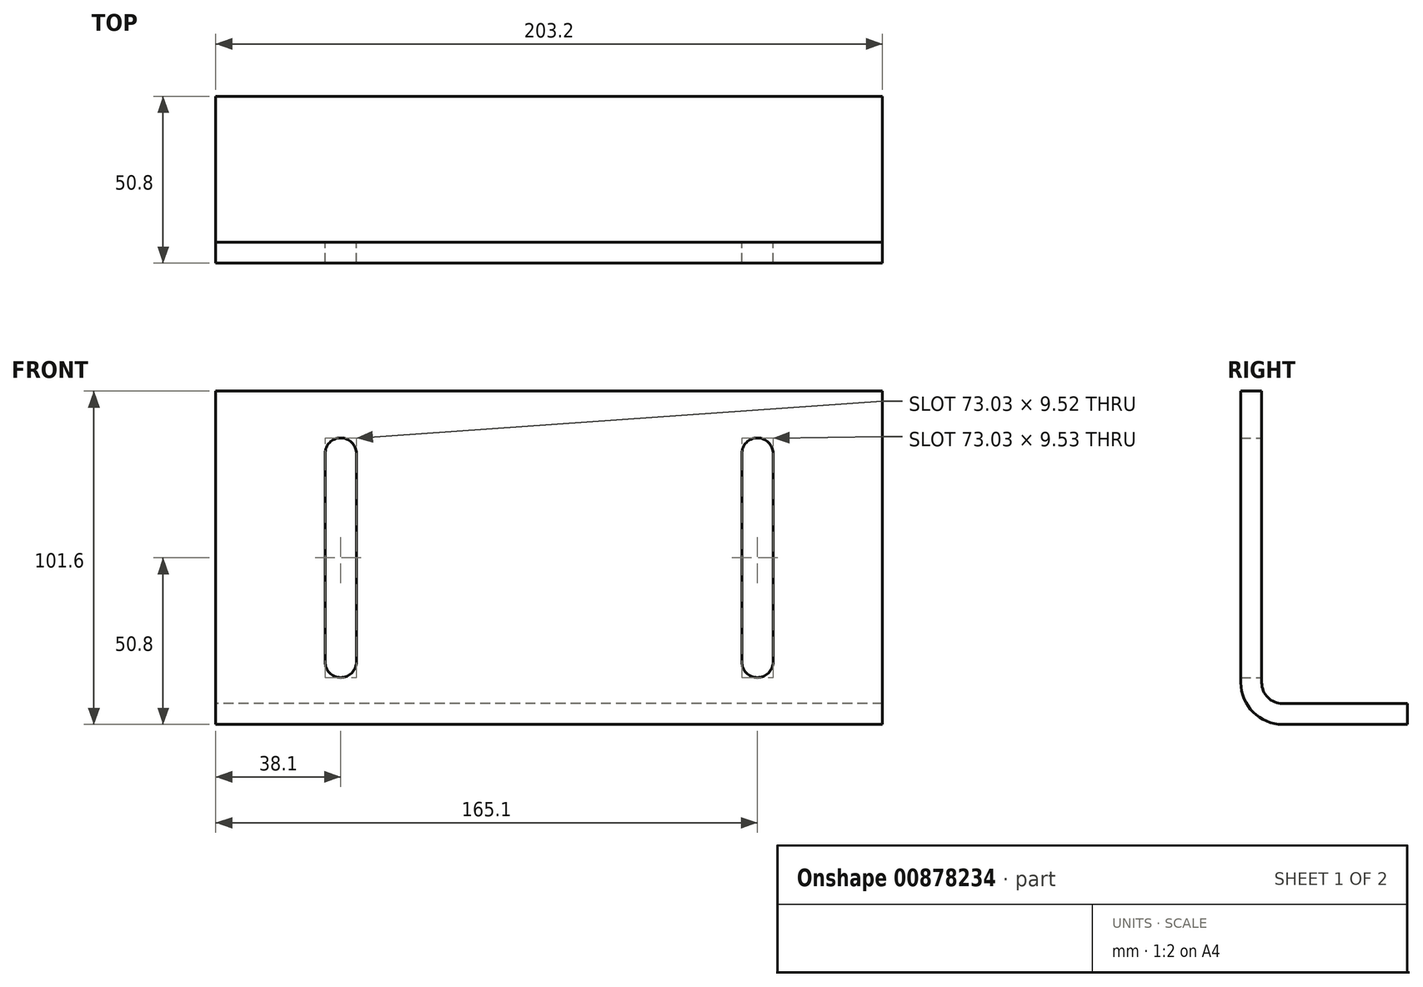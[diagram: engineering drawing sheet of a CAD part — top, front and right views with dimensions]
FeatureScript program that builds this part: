
annotation { "Feature Type Name" : "Feature", "Feature Type Description" : "" }
export const myFeature = defineFeature(function(context is Context, id is Id, definition is map)
    precondition{}
    {
        {
            var Q0;
            Q0=qCreatedBy(makeId("Right.planeOp"),FACE);
            var sketch = newSketch(context, id + "F0", { "sketchPlane" : qUnion([Q0])});
            skLineSegment(sketch, "E0.top", {"start": v(-6.35, 95.25) * mm, "end": v(0, 95.25) * mm});
            skLineSegment(sketch, "E0.left", {"start": v(-6.35, 6.35) * mm, "end": v(-6.35, 95.25) * mm});
            skLineSegment(sketch, "E0.right", {"start": v(0, 6.35) * mm, "end": v(0, 95.25) * mm});
            skLineSegment(sketch, "E1.bottom", {"start": v(6.35, 0) * mm, "end": v(44.45, 0) * mm});
            skLineSegment(sketch, "E1.top", {"start": v(6.35, -6.35) * mm, "end": v(44.45, -6.35) * mm});
            skLineSegment(sketch, "E1.right", {"start": v(44.45, 0) * mm, "end": v(44.45, -6.35) * mm});
            skPoint(sketch, "E2.visualSharp", {"position": v(0, 0) * mm});
            skArc(sketch, "E2.filletArc", {"start": v(0, 6.35) * mm, "mid": v(1.86, 1.86) * mm, "end": v(6.35, 0) * mm});
            skArc(sketch, "E3.filletArc", {"start": v(-6.35, 6.35) * mm, "mid": v(-2.63, -2.63) * mm, "end": v(6.35, -6.35) * mm});
            skSolve(sketch);
        }
        {
            var Q0;
            Q0 = qSketchRegion(id + "F0", true);
            extrude(context, id + "F1", {"entities" : qUnion([Q0]), "depth" : 203.2 * mm, "offsetDistance" : 25.4 * mm});
        }
        {
            var Q0;
            Q0=makeQuery(id+"F1.opExtrude","SWEPT_FACE",FACE,{"disambiguationData":[OSD([sQuery(id+"F0.wireOp",EDGE,"E0.right")])]});
            var sketch = newSketch(context, id + "F2", { "sketchPlane" : qUnion([Q0])});
            skLineSegment(sketch, "E4", {"start": v(-101.6, 95.25) * mm, "end": v(-101.6, 6.35) * mm, "construction": true});
            skArc(sketch, "E5", {"start": v(-160.34, 76.2) * mm, "mid": v(-165.1, 80.96) * mm, "end": v(-169.86, 76.2) * mm});
            skLineSegment(sketch, "E6", {"start": v(-169.86, 76.2) * mm, "end": v(-169.86, 12.7) * mm});
            skLineSegment(sketch, "E7", {"start": v(-160.34, 76.2) * mm, "end": v(-160.34, 12.7) * mm});
            skArc(sketch, "E8", {"start": v(-169.86, 12.7) * mm, "mid": v(-165.1, 7.94) * mm, "end": v(-160.34, 12.7) * mm});
            skLineSegment(sketch, "E9.MirrorCS", {"start": v(-33.34, 76.2) * mm, "end": v(-33.34, 12.7) * mm});
            skArc(sketch, "E10.MirrorCS", {"start": v(-42.86, 76.2) * mm, "mid": v(-38.1, 80.96) * mm, "end": v(-33.34, 76.2) * mm});
            skLineSegment(sketch, "E11.MirrorCS", {"start": v(-42.86, 76.2) * mm, "end": v(-42.86, 12.7) * mm});
            skArc(sketch, "E12.MirrorCS", {"start": v(-33.34, 12.7) * mm, "mid": v(-38.1, 7.94) * mm, "end": v(-42.86, 12.7) * mm});
            skSolve(sketch);
        }
        {
            var Q0;
            Q0=makeQuery(id+"F2.imprint","IMPRINT",FACE,{"disambiguationData":[TD([[makeQuery(id+"F2.imprint","IMPRINT",EDGE,{"derivedFrom":sQuery(id+"F2.wireOp",EDGE,"E5")}),1.0]])]});
            var Q1;
            Q1=makeQuery(id+"F2.imprint","IMPRINT",FACE,{"disambiguationData":[TD([[makeQuery(id+"F2.imprint","IMPRINT",EDGE,{"derivedFrom":sQuery(id+"F2.wireOp",EDGE,"E9.MirrorCS")}),-1.0]])]});
            extrude(context, id + "F3", {"entities" : qUnion([Q0, Q1]), "operationType" : NewBodyOperationType.REMOVE, "endBound" : BoundingType.THROUGH_ALL, "oppositeDirection" : true, "depth" : 25.4 * mm, "offsetDistance" : 25.4 * mm});
        }
    });
